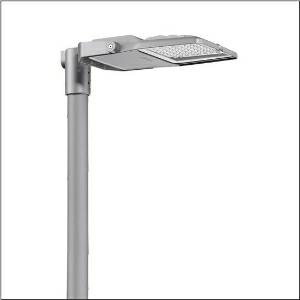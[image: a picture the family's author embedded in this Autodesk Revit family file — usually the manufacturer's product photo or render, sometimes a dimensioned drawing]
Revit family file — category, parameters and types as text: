
# Revit family: floodlight_fl_21_iq_mini___pl52_5xa7772b4d3a_2373
name_source: partatom
category: Lighting Fixtures
units: mm (PartAtom-declared; Revit-internal decimal feet)

## family parameters
Cut with Voids When Loaded = No
Host = Face
Light Source = No
Part Type = Normal
Room Calculation Point = No
Round Connector Dimension = Use Diameter
Shared = No

## types (1)
- --- (1 x LED, 6490 lm, 45.5 W, 4000K)
    Apparent Load = 46 VA
    CIE Flux Codes = 26 60 98 100 100
    Color Rendering = 70
    Color Temperature = 4000K
    Default Elevation = 1800 mm
    Description = Floodlight FL 21 iQ mini, floodlight, primary light control with lens, of PMMA, primary optical cover: protective disc, of toughened safety glass, transparent, light distribution: PL52, light emission: direct distribution, installation type: surface-mounted, LED, High Power LED, rated luminous flux: 6.490lm, luminous efficacy: 143lm/W, light colour: 740, colour temperature: 4000K, control gear: iQ Street-Remote/DALI, control: Auto-Match, Temp-Guard, Night-Set, Smart-Wire, Desk-Remote (wireless, voltage-free reading and setting of iQ features in the workshop via application-optimized NFC function/RFID function), optimised constant luminous flux control (CLO 2.0), Light-Fading, Lumen-Switch, with terminal, 6-pole, mains connection: 220..240V, AC, 50/60Hz, start of lifetime: 46W, end of service life: 48W, reduction: 22W, luminaire housing, of diecast aluminium, powder-coated, Siteco® metallic grey (DB 702S), corrosivity category C5 mid according to DIN EN ISO 12944, suitable for swimming pools, chlorine-resistant, sealing non-destructively replaceable, please order mast flange separately, mast bracket, of steel, galvanised, powder-coated, protection rating (complete): IP66, insulation class (complete): insulation class II (safety insulation), certification: CE, ENEC, VDE, protection symbol: D, impact resistance: IK08, permissible operating ambient temperature: -40..+40°C, permissible operating ambient temperature for outdoor applications: -40..+50°C, standard: DIN EN 12944, LABS conformity tested according to VDMA 24364:2018-05, packaging unit: 1 piece

Light Distribution: PL52
    Height = 70 mm
    Lamp = 1 x LED
    Lamp Light Flux = 6490 lm
    Lamp Power = 45.5 W
    Lamp count = 1
    Length = 485 mm
    Luminous efficacy = 143 lm/W
    Manufacturer = Siteco
    ModVariant = No
    Model = 5XA7772B4D3A
    Number of Poles = 1
    OnlyDefault = Yes
    Power Factor = 1
    Product Name = Floodlight FL 21 iQ mini | PL52
    Product group = floodlight | pylon annexe
    ProductGroupID = 6201
    Protection Class = Protection class II
    Protection Degree = IP 66
    RLX_Detail_Level = 1
    RLX_Emergency_Light_Flux = 0 lm
    RLX_Emergency_Type = 0
    RLX_Emergency_Type_DB = No
    RlxData = <blob elided: 101397 chars, md5=f3d4b946>
    Socket = socket
    Standby Power = 0 W
    System Light Flux = 6490 lm
    System Power = 46 W
    Type Comments = factory setting: luminous flux: 100 % | dim-lin: 254 | 463 mA
    Type Image = l_1007125.jpg
    URL = http://relux.com
    VarID = @adj_186157
    Voltage = 0 V
    Weight = 0.00 kg
    Width = 337 mm

## geometry (parser evidence)
native form markers: Blend x4, Sweep x12
no freeform markers — native parametric forms only
